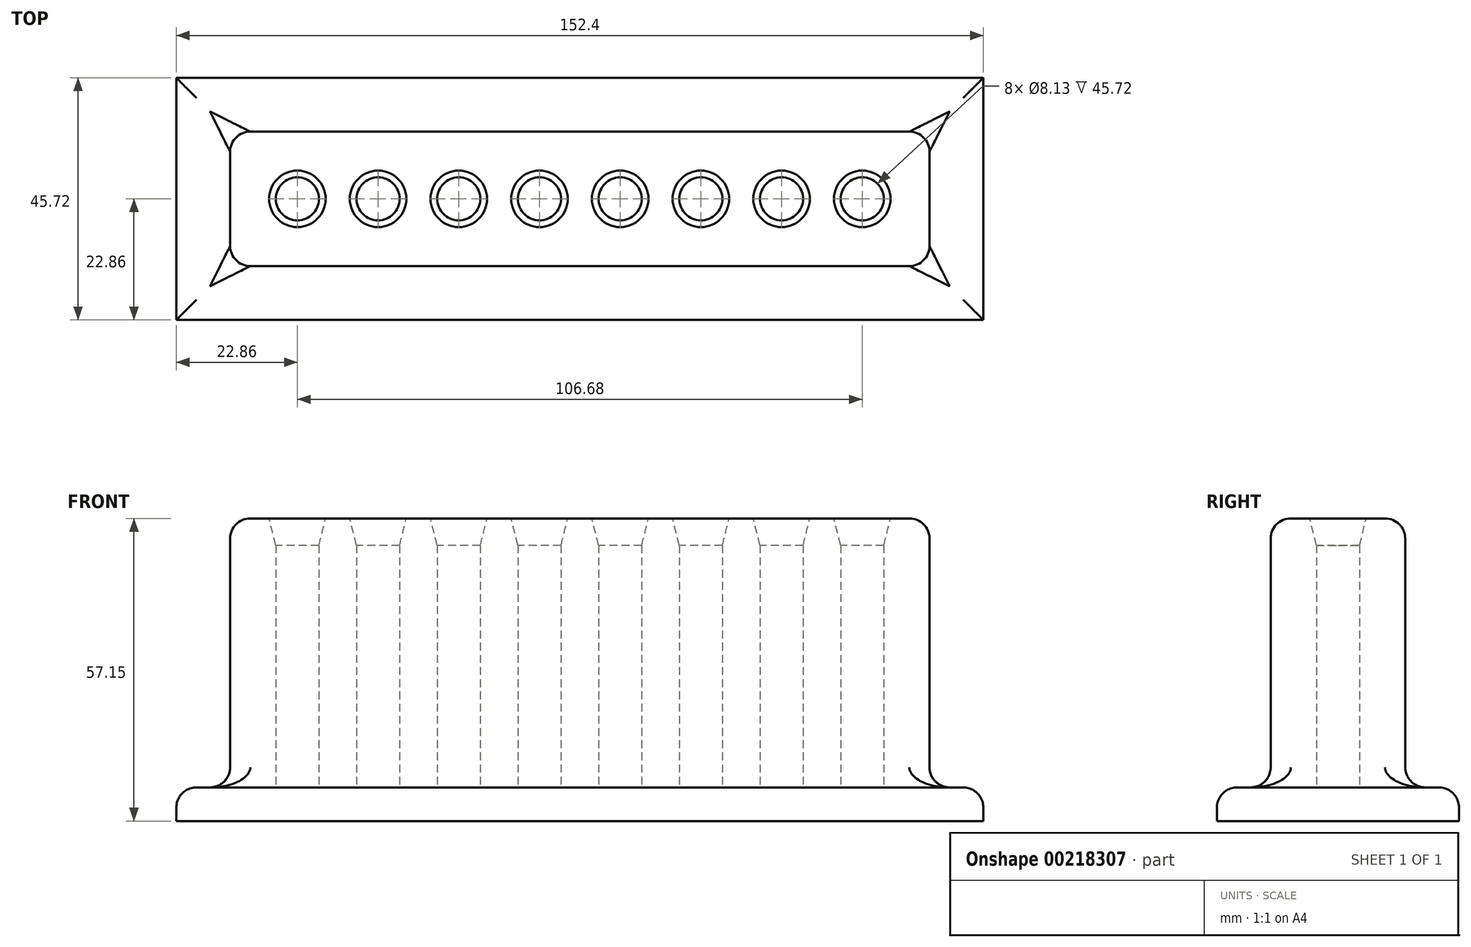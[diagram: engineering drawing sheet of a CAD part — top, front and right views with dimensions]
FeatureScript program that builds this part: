
annotation { "Feature Type Name" : "Feature", "Feature Type Description" : "" }
export const myFeature = defineFeature(function(context is Context, id is Id, definition is map)
    precondition{}
    {
        {
            var Q0;
            Q0=qCreatedBy(makeId("Top.planeOp"),FACE);
            var sketch = newSketch(context, id + "F0", { "sketchPlane" : qUnion([Q0])});
            skLineSegment(sketch, "E0.bottom", {"start": v(66.04, 12.7) * mm, "end": v(-66.04, 12.7) * mm});
            skLineSegment(sketch, "E0.top", {"start": v(66.04, -12.7) * mm, "end": v(-66.04, -12.7) * mm});
            skLineSegment(sketch, "E0.left", {"start": v(66.04, 12.7) * mm, "end": v(66.04, -12.7) * mm});
            skLineSegment(sketch, "E0.right", {"start": v(-66.04, 12.7) * mm, "end": v(-66.04, -12.7) * mm});
            skPoint(sketch, "E0.middle", {"position": v(0, 0) * mm});
            skCircle(sketch, "E1", {"center": v(-53.34, 0) * mm, "radius": 4.06 * mm});
            skCircle(sketch, "E2.1.0.0", {"center": v(-38.1, 0) * mm, "radius": 4.06 * mm});
            skCircle(sketch, "E2.2.0.0", {"center": v(-22.86, 0) * mm, "radius": 4.06 * mm});
            skCircle(sketch, "E2.3.0.0", {"center": v(-7.62, 0) * mm, "radius": 4.06 * mm});
            skCircle(sketch, "E2.4.0.0", {"center": v(7.62, 0) * mm, "radius": 4.06 * mm});
            skCircle(sketch, "E2.5.0.0", {"center": v(22.86, 0) * mm, "radius": 4.06 * mm});
            skLineSegment(sketch, "E2.direction1", {"start": v(-53.34, 0) * mm, "end": v(-38.1, 0) * mm, "construction": true});
            skCircle(sketch, "E3.0.6.0", {"center": v(38.1, 0) * mm, "radius": 4.06 * mm});
            skCircle(sketch, "E3.0.7.0", {"center": v(53.34, 0) * mm, "radius": 4.06 * mm});
            skSolve(sketch);
        }
        {
            var Q0;
            Q0=qSketchRegion(id+"F0",true);
            extrude(context, id + "F1", {"entities" : qUnion([Q0]), "depth" : 50.8 * mm});
        }
        {
            var Q0;
            Q0=makeQuery(id+"F0.imprint","IMPRINT",FACE,{"disambiguationData":[TD([[makeQuery(id+"F0.imprint","IMPRINT",EDGE,{"derivedFrom":sQuery(id+"F0.wireOp",EDGE,"E0.bottom")}),1.0]])]});
            var sketch = newSketch(context, id + "F2", { "sketchPlane" : qUnion([Q0])});
            skLineSegment(sketch, "E4.bottom", {"start": v(76.2, -22.86) * mm, "end": v(-76.2, -22.86) * mm});
            skLineSegment(sketch, "E4.top", {"start": v(76.2, 22.86) * mm, "end": v(-76.2, 22.86) * mm});
            skLineSegment(sketch, "E4.left", {"start": v(76.2, -22.86) * mm, "end": v(76.2, 22.86) * mm});
            skLineSegment(sketch, "E4.right", {"start": v(-76.2, -22.86) * mm, "end": v(-76.2, 22.86) * mm});
            skPoint(sketch, "E4.middle", {"position": v(0, 0) * mm});
            skSolve(sketch);
        }
        {
            var Q0;
            Q0=qSketchRegion(id+"F2",true);
            extrude(context, id + "F3", {"entities" : qUnion([Q0]), "operationType" : NewBodyOperationType.ADD, "oppositeDirection" : true, "depth" : 6.35 * mm});
        }
        {
            var Q0;
            {var subQ0=sQuery(id+"F2.wireOp",EDGE,"E4.bottom");var subQ1=sQuery(id+"F2.wireOp",EDGE,"E4.top");var subQ2=sQuery(id+"F2.wireOp",EDGE,"E4.left");var subQ3=sQuery(id+"F2.wireOp",EDGE,"E4.right");Q0=makeQuery(id+"F3.boolean.opBoolean","SPLIT",FACE,{"disambiguationData":[TD([makeQuery(id+"F1.opExtrude","SWEPT_FACE",FACE,{"disambiguationData":[OSD([sQuery(id+"F0.wireOp",EDGE,"E0.bottom")])]})])],"derivedFrom":makeQuery(id+"F3.opExtrude","CAP_FACE",FACE,{"disambiguationData":[OSD([subQ0,subQ1,subQ2,subQ3])],"isStart":true})});}
            fillet(context, id + "F4", {"entities" : qUnion([Q0]), "radius" : 3.8 * mm, "tangentPropagation" : true, "allowEdgeOverflow" : false});
        }
        {
            var Q0;
            Q0=makeQuery(id+"F1.opExtrude","SWEPT_EDGE",EDGE,{"disambiguationData":[OSD([sQuery(id+"F0.wireOp",EDGE,"E0.bottom"),sQuery(id+"F0.wireOp",EDGE,"E0.right")])]});
            var Q1;
            Q1=makeQuery(id+"F1.opExtrude","SWEPT_EDGE",EDGE,{"disambiguationData":[OSD([sQuery(id+"F0.wireOp",EDGE,"E0.top"),sQuery(id+"F0.wireOp",EDGE,"E0.right")])]});
            var Q2;
            Q2=makeQuery(id+"F1.opExtrude","SWEPT_EDGE",EDGE,{"disambiguationData":[OSD([sQuery(id+"F0.wireOp",EDGE,"E0.top"),sQuery(id+"F0.wireOp",EDGE,"E0.left")])]});
            var Q3;
            Q3=makeQuery(id+"F1.opExtrude","SWEPT_EDGE",EDGE,{"disambiguationData":[OSD([sQuery(id+"F0.wireOp",EDGE,"E0.bottom"),sQuery(id+"F0.wireOp",EDGE,"E0.left")])]});
            var Q4;
            Q4=makeQuery(id+"F1.opExtrude","CAP_EDGE",EDGE,{"disambiguationData":[OSD([sQuery(id+"F0.wireOp",EDGE,"E0.left")])],"isStart":false});
            var Q5;
            Q5=makeQuery(id+"F1.opExtrude","CAP_EDGE",EDGE,{"disambiguationData":[OSD([sQuery(id+"F0.wireOp",EDGE,"E0.bottom")])],"isStart":false});
            var Q6;
            Q6=makeQuery(id+"F1.opExtrude","CAP_EDGE",EDGE,{"disambiguationData":[OSD([sQuery(id+"F0.wireOp",EDGE,"E0.right")])],"isStart":false});
            var Q7;
            Q7=makeQuery(id+"F1.opExtrude","CAP_EDGE",EDGE,{"disambiguationData":[OSD([sQuery(id+"F0.wireOp",EDGE,"E0.top")])],"isStart":false});
            fillet(context, id + "F5", {"entities" : qUnion([Q0, Q1, Q2, Q3, Q4, Q5, Q6, Q7]), "radius" : 3.8 * mm, "tangentPropagation" : true, "allowEdgeOverflow" : false});
        }
        {
            var Q0;
            Q0=makeQuery(id+"F1.opExtrude","CAP_EDGE",EDGE,{"disambiguationData":[OSD([sQuery(id+"F0.wireOp",EDGE,"E2.5.0.0")])],"isStart":false});
            var Q1;
            Q1=makeQuery(id+"F1.opExtrude","CAP_EDGE",EDGE,{"disambiguationData":[OSD([sQuery(id+"F0.wireOp",EDGE,"E2.4.0.0")])],"isStart":false});
            var Q2;
            Q2=makeQuery(id+"F1.opExtrude","CAP_EDGE",EDGE,{"disambiguationData":[OSD([sQuery(id+"F0.wireOp",EDGE,"E2.3.0.0")])],"isStart":false});
            var Q3;
            Q3=makeQuery(id+"F1.opExtrude","CAP_EDGE",EDGE,{"disambiguationData":[OSD([sQuery(id+"F0.wireOp",EDGE,"E2.2.0.0")])],"isStart":false});
            var Q4;
            Q4=makeQuery(id+"F1.opExtrude","CAP_EDGE",EDGE,{"disambiguationData":[OSD([sQuery(id+"F0.wireOp",EDGE,"E2.1.0.0")])],"isStart":false});
            var Q5;
            Q5=makeQuery(id+"F1.opExtrude","CAP_EDGE",EDGE,{"disambiguationData":[OSD([sQuery(id+"F0.wireOp",EDGE,"E1")])],"isStart":false});
            var Q6;
            Q6=makeQuery(id+"F1.opExtrude","CAP_EDGE",EDGE,{"disambiguationData":[OSD([sQuery(id+"F0.wireOp",EDGE,"E3.0.6.0")])],"isStart":false});
            var Q7;
            Q7=makeQuery(id+"F1.opExtrude","CAP_EDGE",EDGE,{"disambiguationData":[OSD([sQuery(id+"F0.wireOp",EDGE,"E3.0.7.0")])],"isStart":false});
            chamfer(context, id + "F6", {"entities" : qUnion([Q0, Q1, Q2, Q3, Q4, Q5, Q6, Q7]), "chamferType" : ChamferType.TWO_OFFSETS, "width1" : 5.08 * mm, "oppositeDirection" : false, "width2" : 1.27 * mm, "tangentPropagation" : true});
        }
    });
